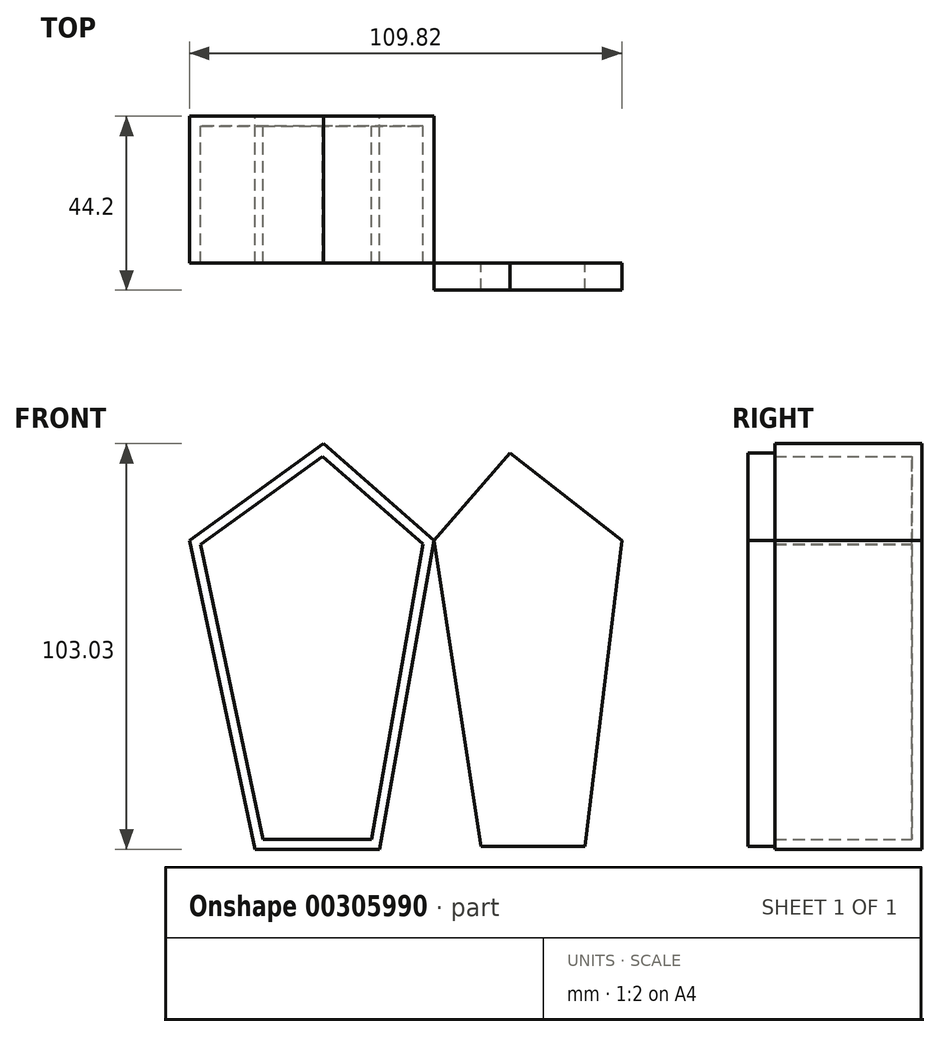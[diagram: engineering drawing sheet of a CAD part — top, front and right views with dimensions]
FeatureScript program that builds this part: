
annotation { "Feature Type Name" : "Feature", "Feature Type Description" : "" }
export const myFeature = defineFeature(function(context is Context, id is Id, definition is map)
    precondition{}
    {
        {
            var Q0;
            Q0=qCreatedBy(makeId("Front.planeOp"),FACE);
            var sketch = newSketch(context, id + "F0", { "sketchPlane" : qUnion([Q0])});
            skLineSegment(sketch, "E0", {"start": v(-45.48, -53.6) * mm, "end": v(-13.78, -53.6) * mm});
            skLineSegment(sketch, "E1", {"start": v(-13.78, -53.6) * mm, "end": v(0, 24.9) * mm});
            skLineSegment(sketch, "E2", {"start": v(0, 24.9) * mm, "end": v(-28.12, 49.44) * mm});
            skLineSegment(sketch, "E3", {"start": v(-28.12, 49.44) * mm, "end": v(-62.08, 24.9) * mm});
            skLineSegment(sketch, "E4", {"start": v(-62.08, 24.9) * mm, "end": v(-45.48, -53.6) * mm});
            skSolve(sketch);
        }
        {
            var Q0;
            Q0 = qSketchRegion(id + "F0", true);
            extrude(context, id + "F1", {"entities" : qUnion([Q0]), "depth" : 37.34 * mm});
        }
        {
            var Q0;
            Q0=makeQuery(id+"F1.opExtrude","CAP_FACE",FACE,{"disambiguationData":[OSD([sQuery(id+"F0.wireOp",EDGE,"E0"),sQuery(id+"F0.wireOp",EDGE,"E1"),sQuery(id+"F0.wireOp",EDGE,"E2"),sQuery(id+"F0.wireOp",EDGE,"E3"),sQuery(id+"F0.wireOp",EDGE,"E4")])],"isStart":false});
            shell(context, id + "F2", {"entities" : qUnion([Q0]), "thickness" : 2.54 * mm});
        }
        {
            var Q0;
            Q0=makeQuery(id+"F1.opExtrude","CAP_FACE",FACE,{"disambiguationData":[OSD([sQuery(id+"F0.wireOp",EDGE,"E0"),sQuery(id+"F0.wireOp",EDGE,"E1"),sQuery(id+"F0.wireOp",EDGE,"E2"),sQuery(id+"F0.wireOp",EDGE,"E3"),sQuery(id+"F0.wireOp",EDGE,"E4")])],"isStart":false});
            var sketch = newSketch(context, id + "F3", { "sketchPlane" : qUnion([Q0])});
            skLineSegment(sketch, "E5", {"start": v(0, 24.9) * mm, "end": v(19.34, 47.07) * mm});
            skLineSegment(sketch, "E6", {"start": v(19.34, 47.07) * mm, "end": v(47.74, 24.9) * mm});
            skLineSegment(sketch, "E7", {"start": v(47.74, 24.9) * mm, "end": v(38.3, -52.84) * mm});
            skLineSegment(sketch, "E8", {"start": v(38.3, -52.84) * mm, "end": v(11.89, -52.84) * mm});
            skLineSegment(sketch, "E9", {"start": v(11.89, -52.84) * mm, "end": v(0, 24.9) * mm});
            skSolve(sketch);
        }
        {
            var Q0;
            Q0=makeQuery(id+"F3.imprint","IMPRINT",FACE,{"disambiguationData":[TD([[makeQuery(id+"F3.imprint","IMPRINT",EDGE,{"derivedFrom":sQuery(id+"F3.wireOp",EDGE,"E5")}),-1.0]])]});
            extrude(context, id + "F4", {"entities" : qUnion([Q0]), "depth" : 6.86 * mm});
        }
    });
